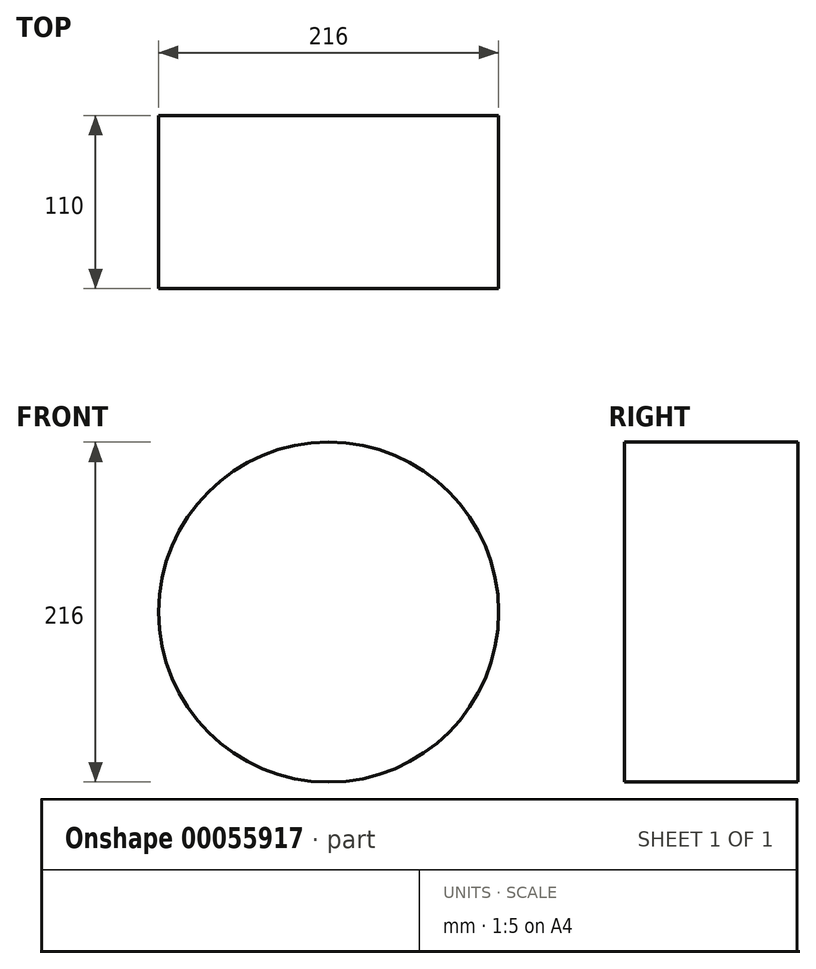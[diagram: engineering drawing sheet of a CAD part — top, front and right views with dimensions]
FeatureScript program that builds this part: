
annotation { "Feature Type Name" : "Feature", "Feature Type Description" : "" }
export const myFeature = defineFeature(function(context is Context, id is Id, definition is map)
    precondition{}
    {
        {
            var Q0;
            Q0=qCreatedBy(makeId("Front.planeOp"),FACE);
            var sketch = newSketch(context, id + "F0", { "sketchPlane" : qUnion([Q0])});
            skCircle(sketch, "E0", {"center": v(0, 0) * mm, "radius": 108 * mm});
            skSolve(sketch);
        }
        {
            var Q0;
            Q0 = qSketchRegion(id + "F0", true);
            extrude(context, id + "F1", {"entities" : qUnion([Q0]), "depth" : 110 * mm});
        }
    });
